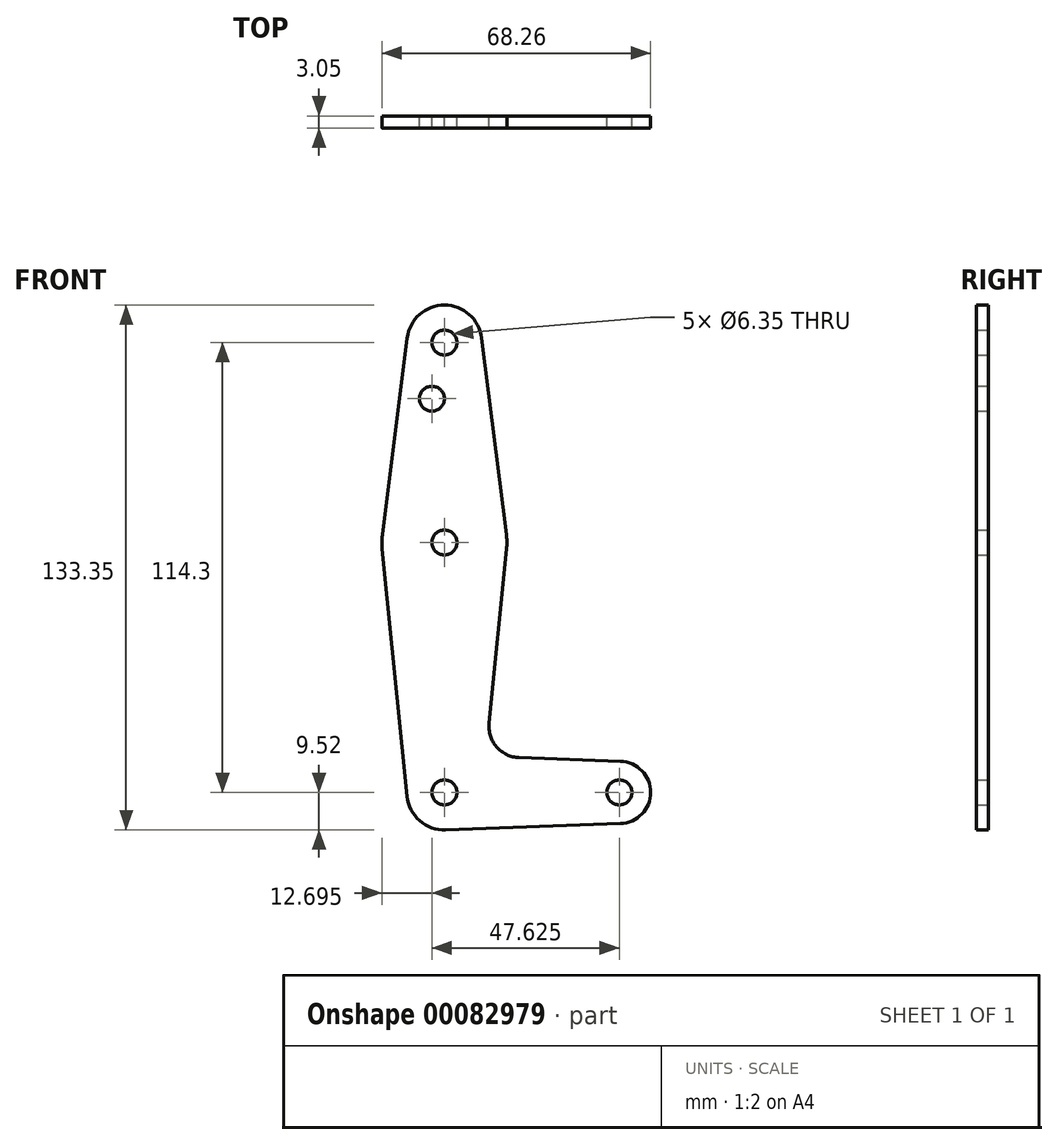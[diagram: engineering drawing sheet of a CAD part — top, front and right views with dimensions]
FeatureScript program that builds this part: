
annotation { "Feature Type Name" : "Feature", "Feature Type Description" : "" }
export const myFeature = defineFeature(function(context is Context, id is Id, definition is map)
    precondition{}
    {
        {
            var Q0;
            Q0=qCreatedBy(makeId("Front.planeOp"),FACE);
            var sketch = newSketch(context, id + "F0", { "sketchPlane" : qUnion([Q0])});
            skLineSegment(sketch, "E0", {"start": v(0, 0) * mm, "end": v(0, 114.3) * mm, "construction": true});
            skLineSegment(sketch, "E1", {"start": v(0, 0) * mm, "end": v(44.45, 0) * mm, "construction": true});
            skCircle(sketch, "E2", {"center": v(0, 0) * mm, "radius": 9.53 * mm});
            skCircle(sketch, "E3", {"center": v(44.45, 0) * mm, "radius": 7.94 * mm});
            skCircle(sketch, "E4", {"center": v(0, 114.3) * mm, "radius": 9.53 * mm});
            skCircle(sketch, "E5", {"center": v(0, 63.5) * mm, "radius": 15.88 * mm});
            skLineSegment(sketch, "E6", {"start": v(-15.75, 65.48) * mm, "end": v(-9.45, 115.5) * mm});
            skLineSegment(sketch, "E7", {"start": v(9.45, 115.5) * mm, "end": v(15.75, 65.48) * mm});
            skLineSegment(sketch, "E8", {"start": v(-15.8, 61.91) * mm, "end": v(-9.48, -0.95) * mm});
            skLineSegment(sketch, "E9", {"start": v(15.8, 61.91) * mm, "end": v(11.34, 17.6) * mm});
            skLineSegment(sketch, "E10", {"start": v(18.97, 8.85) * mm, "end": v(44.73, 7.93) * mm});
            skLineSegment(sketch, "E11", {"start": v(0.34, -9.52) * mm, "end": v(44.73, -7.93) * mm});
            skCircle(sketch, "E12", {"center": v(0, 114.3) * mm, "radius": 3.18 * mm});
            skCircle(sketch, "E13", {"center": v(0, 63.5) * mm, "radius": 3.18 * mm});
            skCircle(sketch, "E14", {"center": v(0, 0) * mm, "radius": 3.18 * mm});
            skCircle(sketch, "E15", {"center": v(44.45, 0) * mm, "radius": 3.18 * mm});
            skCircle(sketch, "E16", {"center": v(-3.18, 100.03) * mm, "radius": 3.18 * mm});
            skArc(sketch, "E17.filletArc", {"start": v(11.34, 17.6) * mm, "mid": v(13.26, 11.57) * mm, "end": v(18.97, 8.85) * mm});
            skSolve(sketch);
        }
        {
            var Q0;
            {var subQ0=sQuery(id+"F0.wireOp",EDGE,"E8");Q0=makeQuery(id+"F0.imprint","IMPRINT",FACE,{"disambiguationData":[TD([[makeQuery(id+"F0.imprint","IMPRINT",EDGE,{"derivedFrom":subQ0}),1.0]])]});}
            var Q1;
            Q1=makeQuery(id+"F0.imprint","IMPRINT",FACE,{"disambiguationData":[TD([[makeQuery(id+"F0.imprint","IMPRINT",EDGE,{"derivedFrom":sQuery(id+"F0.wireOp",EDGE,"E14")}),-1.0]])]});
            var Q2;
            Q2=makeQuery(id+"F0.imprint","IMPRINT",FACE,{"disambiguationData":[TD([[makeQuery(id+"F0.imprint","IMPRINT",EDGE,{"derivedFrom":sQuery(id+"F0.wireOp",EDGE,"E15")}),-1.0]])]});
            var Q3;
            Q3=makeQuery(id+"F0.imprint","IMPRINT",FACE,{"disambiguationData":[TD([[makeQuery(id+"F0.imprint","IMPRINT",EDGE,{"derivedFrom":sQuery(id+"F0.wireOp",EDGE,"E13")}),-1.0]])]});
            var Q4;
            {var subQ1=sQuery(id+"F0.wireOp",EDGE,"E6");Q4=makeQuery(id+"F0.imprint","IMPRINT",FACE,{"disambiguationData":[TD([[makeQuery(id+"F0.imprint","IMPRINT",EDGE,{"derivedFrom":subQ1}),-1.0]])]});}
            var Q5;
            Q5=makeQuery(id+"F0.imprint","IMPRINT",FACE,{"disambiguationData":[TD([[makeQuery(id+"F0.imprint","IMPRINT",EDGE,{"derivedFrom":sQuery(id+"F0.wireOp",EDGE,"E12")}),-1.0]])]});
            extrude(context, id + "F1", {"entities" : qUnion([Q0, Q1, Q2, Q3, Q4, Q5]), "depth" : 3.05 * mm});
        }
    });
